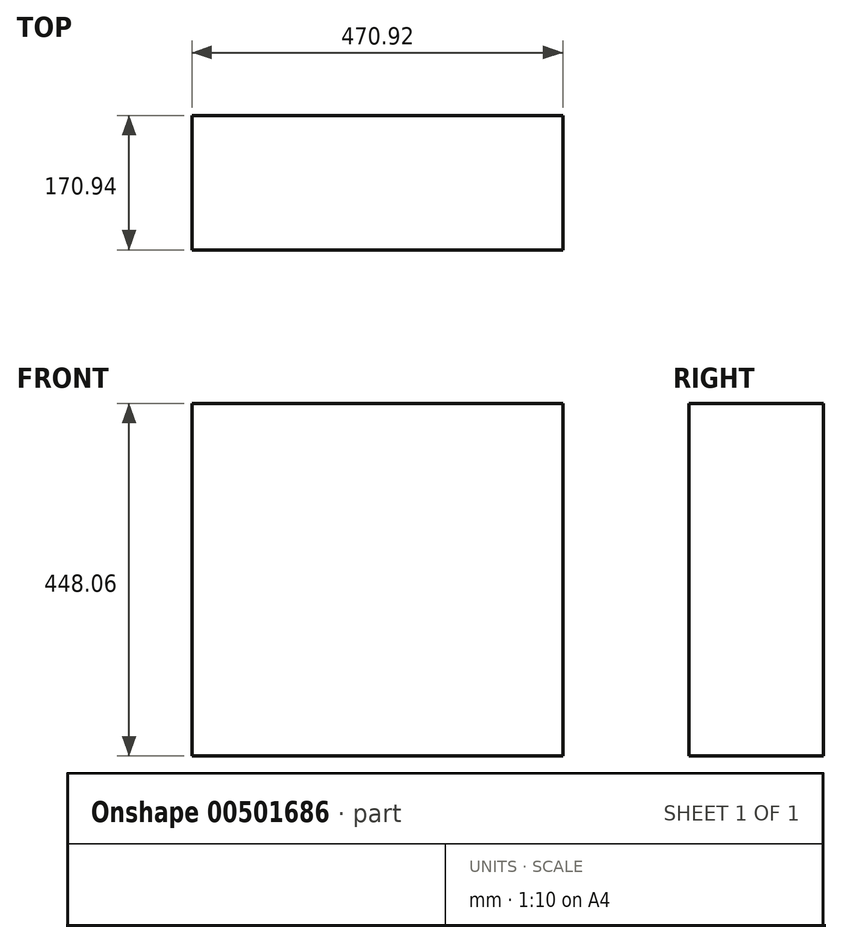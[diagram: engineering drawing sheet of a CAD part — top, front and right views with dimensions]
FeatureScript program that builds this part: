
annotation { "Feature Type Name" : "Feature", "Feature Type Description" : "" }
export const myFeature = defineFeature(function(context is Context, id is Id, definition is map)
    precondition{}
    {
        {
            var Q0;
            Q0=qCreatedBy(makeId("Front.planeOp"),FACE);
            var sketch = newSketch(context, id + "F0", { "sketchPlane" : qUnion([Q0])});
            skLineSegment(sketch, "E0.bottom", {"start": v(0, 0) * mm, "end": v(470.92, 0) * mm});
            skLineSegment(sketch, "E0.top", {"start": v(0, 448.06) * mm, "end": v(470.92, 448.06) * mm});
            skLineSegment(sketch, "E0.left", {"start": v(0, 0) * mm, "end": v(0, 448.06) * mm});
            skLineSegment(sketch, "E0.right", {"start": v(470.92, 0) * mm, "end": v(470.92, 448.06) * mm});
            skSolve(sketch);
        }
        {
            var Q0;
            Q0=makeQuery(id+"F0.imprint","IMPRINT",FACE,{"disambiguationData":[TD([[makeQuery(id+"F0.imprint","IMPRINT",EDGE,{"derivedFrom":sQuery(id+"F0.wireOp",EDGE,"E0.bottom")}),1.0]])]});
            extrude(context, id + "F1", {"entities" : qUnion([Q0]), "depth" : 170.94 * mm});
        }
    });
